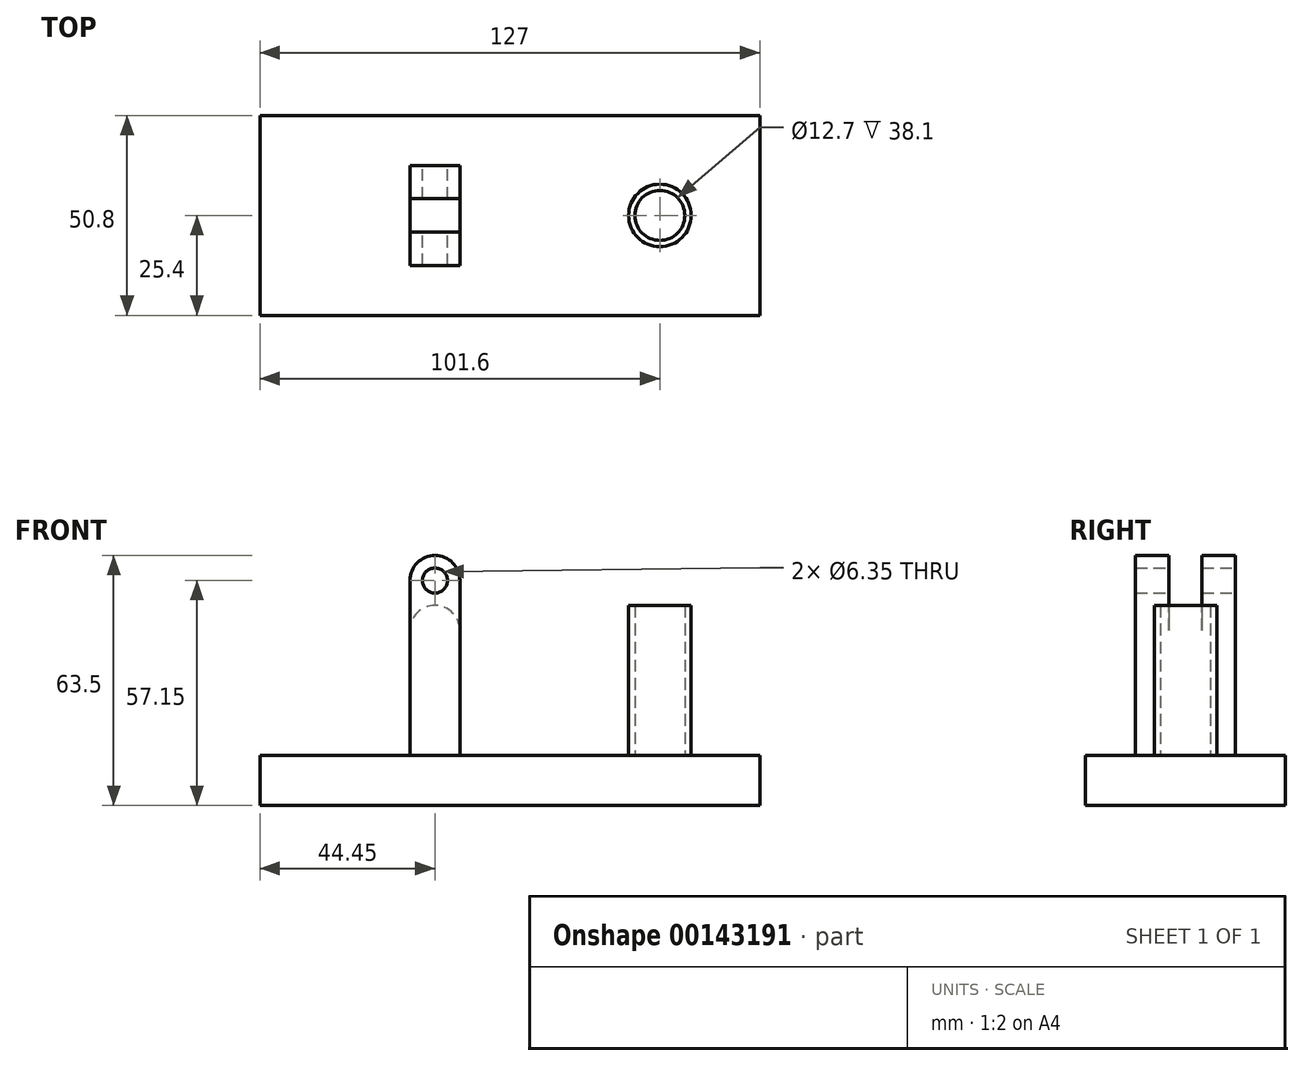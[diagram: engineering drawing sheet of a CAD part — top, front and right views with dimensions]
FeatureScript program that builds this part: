
annotation { "Feature Type Name" : "Feature", "Feature Type Description" : "" }
export const myFeature = defineFeature(function(context is Context, id is Id, definition is map)
    precondition{}
    {
        {
            var Q0;
            Q0=qCreatedBy(makeId("Top.planeOp"),FACE);
            var sketch = newSketch(context, id + "F0", { "sketchPlane" : qUnion([Q0])});
            skLineSegment(sketch, "E0.bottom", {"start": v(0, 0) * mm, "end": v(-127, 0) * mm});
            skLineSegment(sketch, "E0.top", {"start": v(0, 50.8) * mm, "end": v(-127, 50.8) * mm});
            skLineSegment(sketch, "E0.left", {"start": v(0, 0) * mm, "end": v(0, 50.8) * mm});
            skLineSegment(sketch, "E0.right", {"start": v(-127, 0) * mm, "end": v(-127, 50.8) * mm});
            skSolve(sketch);
        }
        {
            var Q0;
            Q0=makeQuery(id+"F0.imprint","IMPRINT",FACE,{"disambiguationData":[TD([[makeQuery(id+"F0.imprint","IMPRINT",EDGE,{"derivedFrom":sQuery(id+"F0.wireOp",EDGE,"E0.bottom")}),-1.0]])]});
            extrude(context, id + "F1", {"entities" : qUnion([Q0]), "depth" : 12.7 * mm});
        }
        {
            var Q0;
            Q0=makeQuery(id+"F1.opExtrude","CAP_FACE",FACE,{"disambiguationData":[OSD([sQuery(id+"F0.wireOp",EDGE,"E0.bottom"),sQuery(id+"F0.wireOp",EDGE,"E0.top"),sQuery(id+"F0.wireOp",EDGE,"E0.left"),sQuery(id+"F0.wireOp",EDGE,"E0.right")])],"isStart":false});
            var sketch = newSketch(context, id + "F2", { "sketchPlane" : qUnion([Q0])});
            skCircle(sketch, "E1", {"center": v(-25.4, 25.4) * mm, "radius": 7.94 * mm});
            skCircle(sketch, "E2", {"center": v(-25.4, 25.4) * mm, "radius": 6.35 * mm});
            skLineSegment(sketch, "E3.bottom", {"start": v(-88.9, 12.7) * mm, "end": v(-76.2, 12.7) * mm});
            skLineSegment(sketch, "E3.top", {"start": v(-88.9, 38.1) * mm, "end": v(-76.2, 38.1) * mm});
            skLineSegment(sketch, "E3.left", {"start": v(-88.9, 12.7) * mm, "end": v(-88.9, 38.1) * mm});
            skLineSegment(sketch, "E3.right", {"start": v(-76.2, 12.7) * mm, "end": v(-76.2, 38.1) * mm});
            skSolve(sketch);
        }
        {
            var Q0;
            Q0=makeQuery(id+"F2.imprint","IMPRINT",FACE,{"disambiguationData":[TD([[makeQuery(id+"F2.imprint","IMPRINT",EDGE,{"derivedFrom":sQuery(id+"F2.wireOp",EDGE,"E1")}),1.0]])]});
            var Q1;
            Q1=makeQuery(id+"F2.imprint","IMPRINT",FACE,{"disambiguationData":[TD([[makeQuery(id+"F2.imprint","IMPRINT",EDGE,{"derivedFrom":sQuery(id+"F2.wireOp",EDGE,"E3.bottom")}),1.0]])]});
            extrude(context, id + "F3", {"entities" : qUnion([Q0, Q1]), "operationType" : NewBodyOperationType.ADD, "depth" : 38.1 * mm});
        }
        {
            var Q0;
            Q0=makeQuery(id+"F3.opExtrude","CAP_FACE",FACE,{"disambiguationData":[OSD([sQuery(id+"F2.wireOp",EDGE,"E3.bottom"),sQuery(id+"F2.wireOp",EDGE,"E3.top"),sQuery(id+"F2.wireOp",EDGE,"E3.left"),sQuery(id+"F2.wireOp",EDGE,"E3.right")])],"isStart":false});
            var sketch = newSketch(context, id + "F4", { "sketchPlane" : qUnion([Q0])});
            skLineSegment(sketch, "E4.bottom", {"start": v(-88.9, 38.1) * mm, "end": v(-76.2, 38.1) * mm});
            skLineSegment(sketch, "E4.top", {"start": v(-88.9, 29.63) * mm, "end": v(-76.2, 29.63) * mm});
            skLineSegment(sketch, "E4.left", {"start": v(-88.9, 38.1) * mm, "end": v(-88.9, 29.63) * mm});
            skLineSegment(sketch, "E4.right", {"start": v(-76.2, 38.1) * mm, "end": v(-76.2, 29.63) * mm});
            skLineSegment(sketch, "E5.bottom", {"start": v(-76.2, 12.7) * mm, "end": v(-88.9, 12.7) * mm});
            skLineSegment(sketch, "E5.top", {"start": v(-76.2, 21.17) * mm, "end": v(-88.9, 21.17) * mm});
            skLineSegment(sketch, "E5.left", {"start": v(-76.2, 12.7) * mm, "end": v(-76.2, 21.17) * mm});
            skLineSegment(sketch, "E5.right", {"start": v(-88.9, 12.7) * mm, "end": v(-88.9, 21.17) * mm});
            skSolve(sketch);
        }
        {
            var Q0;
            Q0=makeQuery(id+"F4.imprint","IMPRINT",FACE,{"disambiguationData":[TD([[makeQuery(id+"F4.imprint","IMPRINT",EDGE,{"derivedFrom":sQuery(id+"F4.wireOp",EDGE,"E4.bottom")}),-1.0]])]});
            var Q1;
            Q1=makeQuery(id+"F4.imprint","IMPRINT",FACE,{"disambiguationData":[TD([[makeQuery(id+"F4.imprint","IMPRINT",EDGE,{"derivedFrom":sQuery(id+"F4.wireOp",EDGE,"E5.bottom")}),1.0]])]});
            extrude(context, id + "F5", {"entities" : qUnion([Q0, Q1]), "operationType" : NewBodyOperationType.ADD, "depth" : 12.7 * mm});
        }
        {
            var Q0;
            Q0=makeQuery(id+"F5.opExtrude","CAP_EDGE",EDGE,{"disambiguationData":[OSD([sQuery(id+"F4.wireOp",EDGE,"E4.left")])],"isStart":false});
            var Q1;
            Q1=makeQuery(id+"F5.opExtrude","CAP_EDGE",EDGE,{"disambiguationData":[OSD([sQuery(id+"F4.wireOp",EDGE,"E5.right")])],"isStart":false});
            var Q2;
            Q2=makeQuery(id+"F5.opExtrude","CAP_EDGE",EDGE,{"disambiguationData":[OSD([sQuery(id+"F4.wireOp",EDGE,"E4.right")])],"isStart":false});
            var Q3;
            Q3=makeQuery(id+"F5.opExtrude","CAP_EDGE",EDGE,{"disambiguationData":[OSD([sQuery(id+"F4.wireOp",EDGE,"E5.left")])],"isStart":false});
            var Q4;
            Q4=makeQuery(id+"F3.opExtrude","CAP_EDGE",EDGE,{"disambiguationData":[OSD([sQuery(id+"F2.wireOp",EDGE,"E3.left")])],"isStart":false});
            var Q5;
            Q5=makeQuery(id+"F3.opExtrude","CAP_EDGE",EDGE,{"disambiguationData":[OSD([sQuery(id+"F2.wireOp",EDGE,"E3.right")])],"isStart":false});
            fillet(context, id + "F6", {"entities" : qUnion([Q0, Q1, Q2, Q3, Q4, Q5]), "radius" : 6.35 * mm, "tangentPropagation" : true, "allowEdgeOverflow" : false});
        }
        {
            var Q0;
            Q0=makeQuery(id+"F5.boolean.opBoolean","MERGE",FACE,{"derivedFrom":[makeQuery(id+"F3.opExtrude","SWEPT_FACE",FACE,{"disambiguationData":[OSD([sQuery(id+"F2.wireOp",EDGE,"E3.top")])]}),makeQuery(id+"F5.opExtrude","SWEPT_FACE",FACE,{"disambiguationData":[OSD([sQuery(id+"F4.wireOp",EDGE,"E4.bottom")])]})]});
            var sketch = newSketch(context, id + "F7", { "sketchPlane" : qUnion([Q0])});
            skCircle(sketch, "E6", {"center": v(82.55, 57.15) * mm, "radius": 3.17 * mm});
            skSolve(sketch);
        }
        {
            var Q0;
            Q0=makeQuery(id+"F7.imprint","IMPRINT",FACE,{"disambiguationData":[TD([[makeQuery(id+"F7.imprint","IMPRINT",EDGE,{"derivedFrom":sQuery(id+"F7.wireOp",EDGE,"E6")}),1.0]])]});
            extrude(context, id + "F8", {"entities" : qUnion([Q0]), "operationType" : NewBodyOperationType.REMOVE, "oppositeDirection" : true, "depth" : 25.4 * mm});
        }
    });
